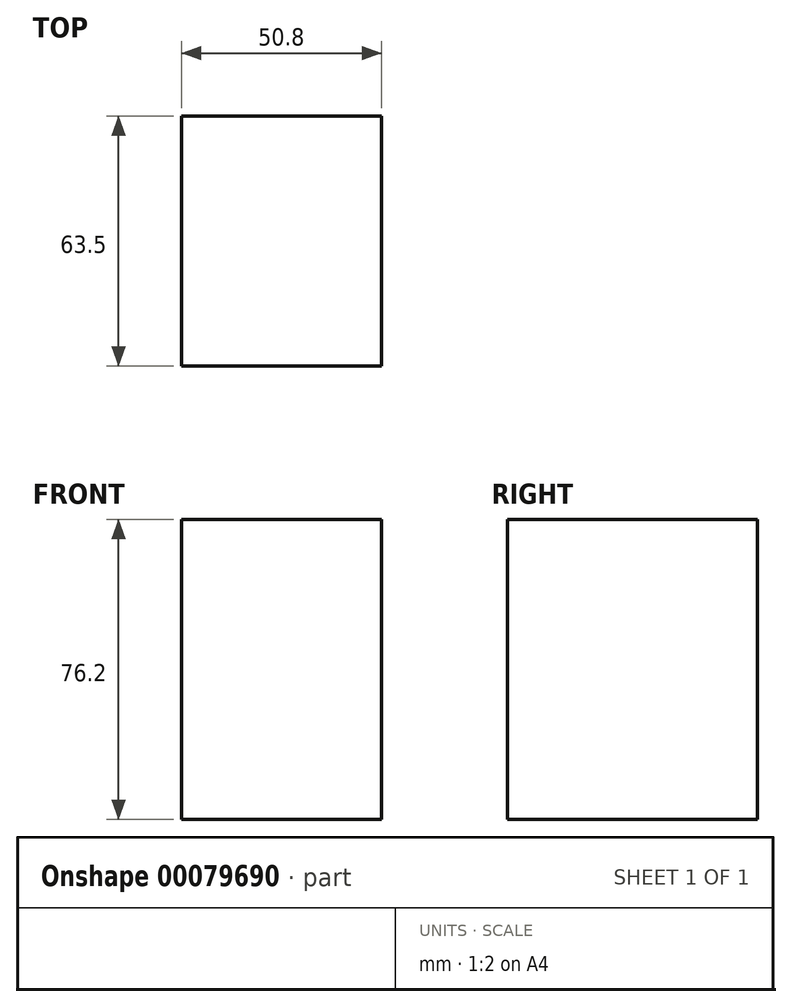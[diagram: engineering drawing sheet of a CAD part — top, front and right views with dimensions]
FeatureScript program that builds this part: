
annotation { "Feature Type Name" : "Feature", "Feature Type Description" : "" }
export const myFeature = defineFeature(function(context is Context, id is Id, definition is map)
    precondition{}
    {
        {
            var Q0;
            Q0=qCreatedBy(makeId("Front.planeOp"),FACE);
            var sketch = newSketch(context, id + "F0", { "sketchPlane" : qUnion([Q0])});
            skLineSegment(sketch, "E0.bottom", {"start": v(0, 0) * mm, "end": v(50.8, 0) * mm});
            skLineSegment(sketch, "E0.top", {"start": v(0, 76.2) * mm, "end": v(50.8, 76.2) * mm});
            skLineSegment(sketch, "E0.left", {"start": v(0, 0) * mm, "end": v(0, 76.2) * mm});
            skLineSegment(sketch, "E0.right", {"start": v(50.8, 0) * mm, "end": v(50.8, 76.2) * mm});
            skSolve(sketch);
        }
        {
            var Q0;
            Q0=makeQuery(id+"F0.imprint","IMPRINT",FACE,{"disambiguationData":[TD([[makeQuery(id+"F0.imprint","IMPRINT",EDGE,{"derivedFrom":sQuery(id+"F0.wireOp",EDGE,"E0.bottom")}),1.0]])]});
            extrude(context, id + "F1", {"entities" : qUnion([Q0]), "endBound" : BoundingType.SYMMETRIC, "depth" : 63.5 * mm});
        }
        {
            var Q0;
            Q0=makeQuery(id+"F1.opExtrude","SWEPT_FACE",FACE,{"disambiguationData":[OSD([sQuery(id+"F0.wireOp",EDGE,"E0.top")])]});
            var sketch = newSketch(context, id + "F2", { "sketchPlane" : qUnion([Q0])});
            skCircle(sketch, "E1", {"center": v(25.4, 0) * mm, "radius": 12.7 * mm});
            skPoint(sketch, "E1.centerSnap0", {"position": v(25.4, 31.75) * mm});
            skSolve(sketch);
        }
        {
            var Q0;
            Q0=sQuery(id+"F2.wireOp",EDGE,"E1");
            extrude(context, id + "F3", {"bodyType" : ToolBodyType.SURFACE, "surfaceEntities" : qUnion([Q0]), "depth" : 25.4 * mm});
        }
    });
